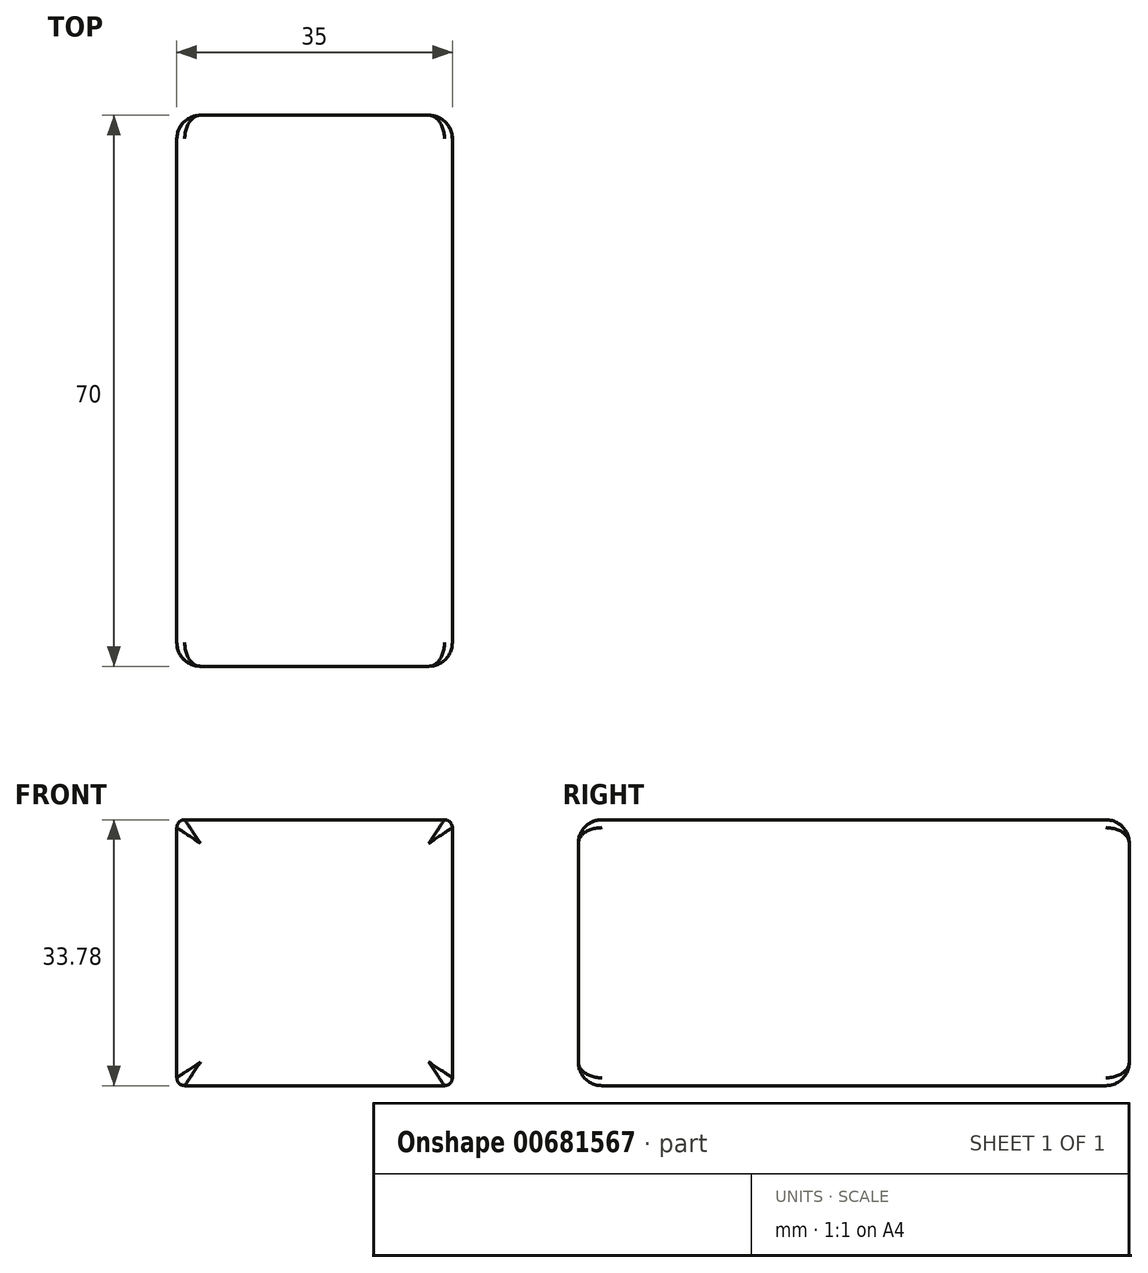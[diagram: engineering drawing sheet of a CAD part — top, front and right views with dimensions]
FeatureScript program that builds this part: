
annotation { "Feature Type Name" : "Feature", "Feature Type Description" : "" }
export const myFeature = defineFeature(function(context is Context, id is Id, definition is map)
    precondition{}
    {
        {
            var Q0;
            Q0=qCreatedBy(makeId("Front.planeOp"),FACE);
            var sketch = newSketch(context, id + "F0", { "sketchPlane" : qUnion([Q0])});
            skLineSegment(sketch, "E0.bottom", {"start": v(16.5, -16.89) * mm, "end": v(-16.5, -16.89) * mm});
            skLineSegment(sketch, "E0.top", {"start": v(16.5, 16.89) * mm, "end": v(-16.5, 16.89) * mm});
            skLineSegment(sketch, "E0.left", {"start": v(17.5, -15.89) * mm, "end": v(17.5, 15.89) * mm});
            skLineSegment(sketch, "E0.right", {"start": v(-17.5, -15.89) * mm, "end": v(-17.5, 15.89) * mm});
            skPoint(sketch, "E0.middle", {"position": v(0, 0) * mm});
            skPoint(sketch, "E1.visualSharp", {"position": v(-17.5, 16.89) * mm});
            skArc(sketch, "E1.filletArc", {"start": v(-16.5, 16.89) * mm, "mid": v(-17.2, 16.6) * mm, "end": v(-17.5, 15.89) * mm});
            skPoint(sketch, "E2.visualSharp", {"position": v(17.5, 16.89) * mm});
            skArc(sketch, "E2.filletArc", {"start": v(17.5, 15.89) * mm, "mid": v(17.2, 16.6) * mm, "end": v(16.5, 16.89) * mm});
            skPoint(sketch, "E3.visualSharp", {"position": v(17.5, -16.89) * mm});
            skArc(sketch, "E3.filletArc", {"start": v(16.5, -16.89) * mm, "mid": v(17.2, -16.6) * mm, "end": v(17.5, -15.89) * mm});
            skPoint(sketch, "E4.visualSharp", {"position": v(-17.5, -16.89) * mm});
            skArc(sketch, "E4.filletArc", {"start": v(-17.5, -15.89) * mm, "mid": v(-17.2, -16.6) * mm, "end": v(-16.5, -16.89) * mm});
            skSolve(sketch);
        }
        {
            var Q0;
            Q0=makeQuery(id+"F0.imprint","IMPRINT",FACE,{"disambiguationData":[TD([[makeQuery(id+"F0.imprint","IMPRINT",EDGE,{"derivedFrom":sQuery(id+"F0.wireOp",EDGE,"E0.bottom")}),-1.0]])]});
            extrude(context, id + "F1", {"entities" : qUnion([Q0]), "endBound" : BoundingType.SYMMETRIC, "depth" : 70 * mm, "offsetDistance" : 25 * mm});
        }
        {
            var Q0;
            Q0=makeQuery(id+"F1.opExtrude","CAP_EDGE",EDGE,{"disambiguationData":[OSD([sQuery(id+"F0.wireOp",EDGE,"E0.top")])],"isStart":false});
            var Q1;
            Q1=makeQuery(id+"F1.opExtrude","CAP_EDGE",EDGE,{"disambiguationData":[OSD([sQuery(id+"F0.wireOp",EDGE,"E0.top")])],"isStart":true});
            fillet(context, id + "F2", {"entities" : qUnion([Q0, Q1]), "tangentPropagation" : true, "radius" : 3 * mm, "defaultsChanged" : true, "vertexSettings" : [], "allowEdgeOverflow" : false});
        }
    });
